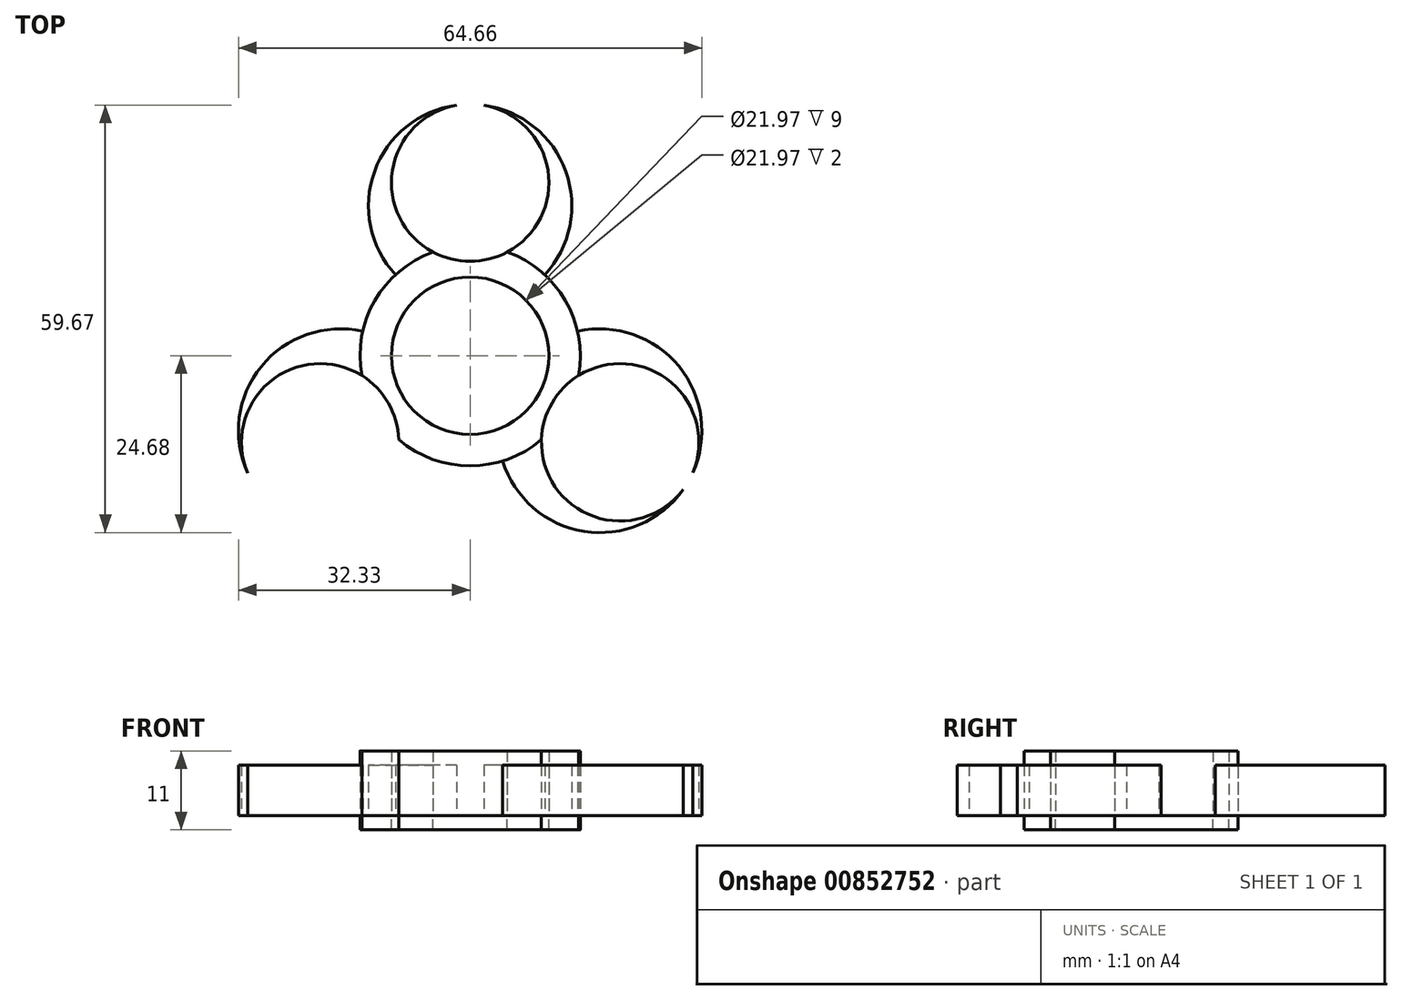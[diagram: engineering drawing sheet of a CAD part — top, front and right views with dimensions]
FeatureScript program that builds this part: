
annotation { "Feature Type Name" : "Feature", "Feature Type Description" : "" }
export const myFeature = defineFeature(function(context is Context, id is Id, definition is map)
    precondition{}
    {
        {
            var Q0;
            Q0=qCreatedBy(makeId("Top.planeOp"),FACE);
            var sketch = newSketch(context, id + "F0", { "sketchPlane" : qUnion([Q0])});
            skCircle(sketch, "E0.cCircle", {"center": v(0, 0) * mm, "radius": 20.93 * mm, "construction": true});
            skLineSegment(sketch, "E0.0", {"start": v(20.93, 12.08) * mm, "end": v(20.93, -12.08) * mm, "construction": true});
            skLineSegment(sketch, "E0.1", {"start": v(20.93, -12.08) * mm, "end": v(0, -24.17) * mm, "construction": true});
            skLineSegment(sketch, "E0.2", {"start": v(0, -24.17) * mm, "end": v(-20.93, -12.08) * mm, "construction": true});
            skLineSegment(sketch, "E0.3", {"start": v(-20.93, -12.08) * mm, "end": v(-20.93, 12.08) * mm, "construction": true});
            skLineSegment(sketch, "E0.4", {"start": v(-20.93, 12.08) * mm, "end": v(0, 24.17) * mm, "construction": true});
            skLineSegment(sketch, "E0.5", {"start": v(0, 24.17) * mm, "end": v(20.93, 12.08) * mm, "construction": true});
            skPoint(sketch, "E0.0.midPoint", {"position": v(20.93, 0) * mm});
            skCircle(sketch, "E1", {"center": v(0, 0) * mm, "radius": 10.99 * mm});
            skLineSegment(sketch, "E2", {"start": v(0, 0) * mm, "end": v(0, 24.17) * mm, "construction": true});
            skLineSegment(sketch, "E3", {"start": v(0, 0) * mm, "end": v(20.93, -12.08) * mm, "construction": true});
            skLineSegment(sketch, "E4", {"start": v(0, 0) * mm, "end": v(-20.93, -12.08) * mm, "construction": true});
            skCircle(sketch, "E5.cCircle", {"center": v(-20.93, -12.08) * mm, "radius": 6.6 * mm, "construction": true});
            skLineSegment(sketch, "E5.0", {"start": v(-20.93, 1.11) * mm, "end": v(-9.5, -18.68) * mm, "construction": true});
            skLineSegment(sketch, "E5.1", {"start": v(-9.5, -18.68) * mm, "end": v(-32.36, -18.68) * mm, "construction": true});
            skLineSegment(sketch, "E5.2", {"start": v(-32.36, -18.68) * mm, "end": v(-20.93, 1.11) * mm, "construction": true});
            skPoint(sketch, "E5.0.midPoint", {"position": v(-15.21, -8.78) * mm});
            skCircle(sketch, "E6.cCircle", {"center": v(0, 24.17) * mm, "radius": 6.6 * mm, "construction": true});
            skLineSegment(sketch, "E6.0", {"start": v(11.43, 17.57) * mm, "end": v(-11.43, 17.57) * mm, "construction": true});
            skLineSegment(sketch, "E6.1", {"start": v(-11.43, 17.57) * mm, "end": v(0, 37.37) * mm, "construction": true});
            skLineSegment(sketch, "E6.2", {"start": v(0, 37.37) * mm, "end": v(11.43, 17.57) * mm, "construction": true});
            skPoint(sketch, "E6.0.midPoint", {"position": v(0, 17.57) * mm});
            skCircle(sketch, "E7.cCircle", {"center": v(20.93, -12.08) * mm, "radius": 6.6 * mm, "construction": true});
            skLineSegment(sketch, "E7.0", {"start": v(9.5, -18.68) * mm, "end": v(20.93, 1.11) * mm, "construction": true});
            skLineSegment(sketch, "E7.1", {"start": v(20.93, 1.11) * mm, "end": v(32.36, -18.68) * mm, "construction": true});
            skLineSegment(sketch, "E7.2", {"start": v(32.36, -18.68) * mm, "end": v(9.5, -18.68) * mm, "construction": true});
            skPoint(sketch, "E7.0.midPoint", {"position": v(15.21, -8.78) * mm});
            skArc(sketch, "E8", {"start": v(-30.58, -17.33) * mm, "mid": v(-30.17, -18.02) * mm, "end": v(-29.71, -18.68) * mm});
            skArc(sketch, "E9", {"start": v(-29.71, -18.68) * mm, "mid": v(-11.69, -6.14) * mm, "end": v(-30.58, -17.33) * mm});
            skArc(sketch, "E10", {"start": v(30.97, -16.54) * mm, "mid": v(11.42, -6.6) * mm, "end": v(29.81, -18.55) * mm});
            skArc(sketch, "E11", {"start": v(29.81, -18.55) * mm, "mid": v(30.44, -17.58) * mm, "end": v(30.97, -16.54) * mm});
            skArc(sketch, "E12", {"start": v(1.9, 34.99) * mm, "mid": v(0.3, 35.15) * mm, "end": v(-1.33, 35.07) * mm});
            skArc(sketch, "E13", {"start": v(-1.33, 35.07) * mm, "mid": v(-0.3, 13.19) * mm, "end": v(1.9, 34.99) * mm});
            skArc(sketch, "E14", {"start": v(-1.31, 35.05) * mm, "mid": v(-0.3, 6.75) * mm, "end": v(1.9, 34.99) * mm});
            skArc(sketch, "E15", {"start": v(-29.71, -18.68) * mm, "mid": v(-5.8, -3.36) * mm, "end": v(-31.04, -16.37) * mm});
            skArc(sketch, "E16", {"start": v(31.03, -16.4) * mm, "mid": v(5.8, -3.35) * mm, "end": v(29.71, -18.68) * mm});
            skPoint(sketch, "E17", {"position": v(-31.04, -16.37) * mm});
            skCircle(sketch, "E18", {"center": v(0, 0) * mm, "radius": 15.37 * mm});
            skSolve(sketch);
        }
        {
            var Q0;
            {var subQ0=sQuery(id+"F0.wireOp",EDGE,"E14");var subQ1=sQuery(id+"F0.wireOp",EDGE,"E13");var subQ2=makeQuery(id+"F0.imprint","INTERSECT",VERTEX,{"derivedFrom":[subQ1,subQ0]});Q0=makeQuery(id+"F0.imprint","IMPRINT",FACE,{"disambiguationData":[TD([[makeQuery(id+"F0.imprint","IMPRINT",EDGE,{"disambiguationData":[TD([[subQ2,-1.0]])],"derivedFrom":subQ1}),-1.0]])]});}
            var Q1;
            {var subQ0=sQuery(id+"F0.wireOp",EDGE,"E14");var subQ3=sQuery(id+"F0.wireOp",EDGE,"E18");var subQ5=makeQuery(id+"F0.imprint","INTERSECT",VERTEX,{"disambiguationData":[OD(1.0)],"derivedFrom":[subQ0,subQ3]});Q1=makeQuery(id+"F0.imprint","IMPRINT",FACE,{"disambiguationData":[TD([[makeQuery(id+"F0.imprint","IMPRINT",EDGE,{"disambiguationData":[TD([[subQ5,-1.0]])],"derivedFrom":subQ3}),-1.0]])]});}
            var Q2;
            {var subQ0=sQuery(id+"F0.wireOp",EDGE,"E15");var subQ1=sQuery(id+"F0.wireOp",EDGE,"E9");var subQ2=makeQuery(id+"F0.imprint","INTERSECT",VERTEX,{"derivedFrom":[subQ1,subQ0]});Q2=makeQuery(id+"F0.imprint","IMPRINT",FACE,{"disambiguationData":[TD([[makeQuery(id+"F0.imprint","IMPRINT",EDGE,{"disambiguationData":[TD([[subQ2,1.0]])],"derivedFrom":subQ1}),-1.0]])]});}
            var Q3;
            {var subQ0=sQuery(id+"F0.wireOp",EDGE,"E15");var subQ3=sQuery(id+"F0.wireOp",EDGE,"E18");var subQ5=makeQuery(id+"F0.imprint","INTERSECT",VERTEX,{"disambiguationData":[OD(0.0)],"derivedFrom":[subQ0,subQ3]});Q3=makeQuery(id+"F0.imprint","IMPRINT",FACE,{"disambiguationData":[TD([[makeQuery(id+"F0.imprint","IMPRINT",EDGE,{"disambiguationData":[TD([[subQ5,1.0]])],"derivedFrom":subQ3}),-1.0]])]});}
            var Q4;
            {var subQ0=sQuery(id+"F0.wireOp",EDGE,"E16");var subQ1=sQuery(id+"F0.wireOp",EDGE,"E10");var subQ2=makeQuery(id+"F0.imprint","INTERSECT",VERTEX,{"disambiguationData":[OD(0.0)],"derivedFrom":[subQ1,subQ0]});Q4=makeQuery(id+"F0.imprint","IMPRINT",FACE,{"disambiguationData":[TD([[makeQuery(id+"F0.imprint","IMPRINT",EDGE,{"disambiguationData":[TD([[subQ2,1.0]])],"derivedFrom":subQ1}),-1.0]])]});}
            var Q5;
            {var subQ0=sQuery(id+"F0.wireOp",EDGE,"E16");var subQ1=sQuery(id+"F0.wireOp",EDGE,"E10");var subQ2=makeQuery(id+"F0.imprint","INTERSECT",VERTEX,{"disambiguationData":[OD(1.0)],"derivedFrom":[subQ1,subQ0]});Q5=makeQuery(id+"F0.imprint","IMPRINT",FACE,{"disambiguationData":[TD([[makeQuery(id+"F0.imprint","IMPRINT",EDGE,{"disambiguationData":[TD([[subQ2,-1.0]])],"derivedFrom":subQ1}),-1.0]])]});}
            extrude(context, id + "F1", {"entities" : qUnion([Q0, Q1, Q2, Q3, Q4, Q5]), "depth" : 7 * mm, "offsetDistance" : 25.4 * mm});
        }
        {
            var Q0;
            {var subQ0=sQuery(id+"F0.wireOp",EDGE,"E14");var subQ1=sQuery(id+"F0.wireOp",EDGE,"E1");var subQ2=makeQuery(id+"F0.imprint","INTERSECT",VERTEX,{"disambiguationData":[OD(1.0)],"derivedFrom":[subQ1,subQ0]});Q0=makeQuery(id+"F0.imprint","IMPRINT",FACE,{"disambiguationData":[TD([[makeQuery(id+"F0.imprint","IMPRINT",EDGE,{"disambiguationData":[TD([[subQ2,-1.0]])],"derivedFrom":subQ1}),-1.0]])]});}
            var Q1;
            {var subQ1=sQuery(id+"F0.wireOp",EDGE,"E15");var subQ3=sQuery(id+"F0.wireOp",EDGE,"E1");var subQ4=makeQuery(id+"F0.imprint","INTERSECT",VERTEX,{"disambiguationData":[OD(0.0)],"derivedFrom":[subQ3,subQ1]});Q1=makeQuery(id+"F0.imprint","IMPRINT",FACE,{"disambiguationData":[TD([[makeQuery(id+"F0.imprint","IMPRINT",EDGE,{"disambiguationData":[TD([[subQ4,-1.0]])],"derivedFrom":subQ3}),-1.0]])]});}
            var Q2;
            {var subQ0=sQuery(id+"F0.wireOp",EDGE,"E15");var subQ1=sQuery(id+"F0.wireOp",EDGE,"E1");var subQ2=makeQuery(id+"F0.imprint","INTERSECT",VERTEX,{"disambiguationData":[OD(1.0)],"derivedFrom":[subQ1,subQ0]});Q2=makeQuery(id+"F0.imprint","IMPRINT",FACE,{"disambiguationData":[TD([[makeQuery(id+"F0.imprint","IMPRINT",EDGE,{"disambiguationData":[TD([[subQ2,-1.0]])],"derivedFrom":subQ1}),-1.0]])]});}
            var Q3;
            {var subQ1=sQuery(id+"F0.wireOp",EDGE,"E16");var subQ3=sQuery(id+"F0.wireOp",EDGE,"E1");var subQ4=makeQuery(id+"F0.imprint","INTERSECT",VERTEX,{"disambiguationData":[OD(0.0)],"derivedFrom":[subQ3,subQ1]});Q3=makeQuery(id+"F0.imprint","IMPRINT",FACE,{"disambiguationData":[TD([[makeQuery(id+"F0.imprint","IMPRINT",EDGE,{"disambiguationData":[TD([[subQ4,1.0]])],"derivedFrom":subQ3}),-1.0]])]});}
            var Q4;
            {var subQ0=sQuery(id+"F0.wireOp",EDGE,"E14");var subQ1=sQuery(id+"F0.wireOp",EDGE,"E1");var subQ2=makeQuery(id+"F0.imprint","INTERSECT",VERTEX,{"disambiguationData":[OD(0.0)],"derivedFrom":[subQ1,subQ0]});Q4=makeQuery(id+"F0.imprint","IMPRINT",FACE,{"disambiguationData":[TD([[makeQuery(id+"F0.imprint","IMPRINT",EDGE,{"disambiguationData":[TD([[subQ2,1.0]])],"derivedFrom":subQ1}),-1.0]])]});}
            var Q5;
            {var subQ1=sQuery(id+"F0.wireOp",EDGE,"E14");var subQ3=sQuery(id+"F0.wireOp",EDGE,"E1");var subQ5=makeQuery(id+"F0.imprint","INTERSECT",VERTEX,{"disambiguationData":[OD(0.0)],"derivedFrom":[subQ3,subQ1]});Q5=makeQuery(id+"F0.imprint","IMPRINT",FACE,{"disambiguationData":[TD([[makeQuery(id+"F0.imprint","IMPRINT",EDGE,{"disambiguationData":[TD([[subQ5,-1.0]])],"derivedFrom":subQ3}),-1.0]])]});}
            extrude(context, id + "F2", {"entities" : qUnion([Q0, Q1, Q2, Q3, Q4, Q5]), "depth" : 9 * mm, "offsetDistance" : 25.4 * mm});
        }
        {
            var Q0;
            {var subQ0=sQuery(id+"F0.wireOp",EDGE,"E14");var subQ1=sQuery(id+"F0.wireOp",EDGE,"E1");var subQ2=makeQuery(id+"F0.imprint","INTERSECT",VERTEX,{"disambiguationData":[OD(0.0)],"derivedFrom":[subQ1,subQ0]});Q0=makeQuery(id+"F0.imprint","IMPRINT",FACE,{"disambiguationData":[TD([[makeQuery(id+"F0.imprint","IMPRINT",EDGE,{"disambiguationData":[TD([[subQ2,1.0]])],"derivedFrom":subQ1}),-1.0]])]});}
            var Q1;
            {var subQ1=sQuery(id+"F0.wireOp",EDGE,"E14");var subQ3=sQuery(id+"F0.wireOp",EDGE,"E1");var subQ5=makeQuery(id+"F0.imprint","INTERSECT",VERTEX,{"disambiguationData":[OD(0.0)],"derivedFrom":[subQ3,subQ1]});Q1=makeQuery(id+"F0.imprint","IMPRINT",FACE,{"disambiguationData":[TD([[makeQuery(id+"F0.imprint","IMPRINT",EDGE,{"disambiguationData":[TD([[subQ5,-1.0]])],"derivedFrom":subQ3}),-1.0]])]});}
            var Q2;
            {var subQ0=sQuery(id+"F0.wireOp",EDGE,"E14");var subQ1=sQuery(id+"F0.wireOp",EDGE,"E1");var subQ2=makeQuery(id+"F0.imprint","INTERSECT",VERTEX,{"disambiguationData":[OD(1.0)],"derivedFrom":[subQ1,subQ0]});Q2=makeQuery(id+"F0.imprint","IMPRINT",FACE,{"disambiguationData":[TD([[makeQuery(id+"F0.imprint","IMPRINT",EDGE,{"disambiguationData":[TD([[subQ2,-1.0]])],"derivedFrom":subQ1}),-1.0]])]});}
            var Q3;
            {var subQ1=sQuery(id+"F0.wireOp",EDGE,"E15");var subQ3=sQuery(id+"F0.wireOp",EDGE,"E1");var subQ4=makeQuery(id+"F0.imprint","INTERSECT",VERTEX,{"disambiguationData":[OD(0.0)],"derivedFrom":[subQ3,subQ1]});Q3=makeQuery(id+"F0.imprint","IMPRINT",FACE,{"disambiguationData":[TD([[makeQuery(id+"F0.imprint","IMPRINT",EDGE,{"disambiguationData":[TD([[subQ4,-1.0]])],"derivedFrom":subQ3}),-1.0]])]});}
            var Q4;
            {var subQ0=sQuery(id+"F0.wireOp",EDGE,"E15");var subQ1=sQuery(id+"F0.wireOp",EDGE,"E1");var subQ2=makeQuery(id+"F0.imprint","INTERSECT",VERTEX,{"disambiguationData":[OD(1.0)],"derivedFrom":[subQ1,subQ0]});Q4=makeQuery(id+"F0.imprint","IMPRINT",FACE,{"disambiguationData":[TD([[makeQuery(id+"F0.imprint","IMPRINT",EDGE,{"disambiguationData":[TD([[subQ2,-1.0]])],"derivedFrom":subQ1}),-1.0]])]});}
            var Q5;
            {var subQ1=sQuery(id+"F0.wireOp",EDGE,"E16");var subQ3=sQuery(id+"F0.wireOp",EDGE,"E1");var subQ4=makeQuery(id+"F0.imprint","INTERSECT",VERTEX,{"disambiguationData":[OD(0.0)],"derivedFrom":[subQ3,subQ1]});Q5=makeQuery(id+"F0.imprint","IMPRINT",FACE,{"disambiguationData":[TD([[makeQuery(id+"F0.imprint","IMPRINT",EDGE,{"disambiguationData":[TD([[subQ4,1.0]])],"derivedFrom":subQ3}),-1.0]])]});}
            extrude(context, id + "F3", {"entities" : qUnion([Q0, Q1, Q2, Q3, Q4, Q5]), "depth" : -2 * mm, "offsetDistance" : 25.4 * mm});
        }
    });
